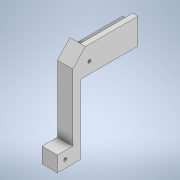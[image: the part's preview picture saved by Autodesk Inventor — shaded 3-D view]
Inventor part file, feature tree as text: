
AUTODESK INVENTOR PART (.ipt)
format: ipt  version: 2020 (Build 240168000, 168)  size: 166,912 bytes
history: native  units: in
note: dims shown in document units (in); Inventor stores cm internally (conversion verified against a paired STEP export)
features: extrude x6, sketch x6
ambient origin geometry x8: Origin, YZ Plane, XZ Plane, XY Plane, X Axis, Y Axis, Z Axis, Center Point
bodies: Solid1 (feature_tree)
feature tree (12):
  extrude  "Extrusion1"  Depth=0.375in
  extrude  "Extrusion3"  Depth=0.75in TaperAngle=0.0deg
  extrude  "Extrusion4"  Depth=0.25in
  extrude  "Extrusion5"  Depth=0.375in
  extrude  "Extrusion6"  Depth=0.5in
  extrude  "Extrusion7"  Depth=0.75in
  sketch  "Sketch1"  dims[d0=1.0in d1=0.375in]
  sketch  "Sketch4"  dims[d3=0.8in d4=0.75in d5=0.0in]
  sketch  "Sketch5"  dims[d11=2.0in d12=0.25in]
  sketch  "Sketch6"  dims[d13=3.0in d14=0.375in]
  sketch  "Sketch7"  dims[d15=0.64in d16=0.0in d17=0.5in]
  sketch  "Sketch8"  dims[d18=0.375in d19=0.0in d20=0.141in d21=3.625in d22=0.0in d23=0.75in d24=0.75in d25=0.75in d26=0.0in d27=0.141in d28=1.25in d29=0.0in]
